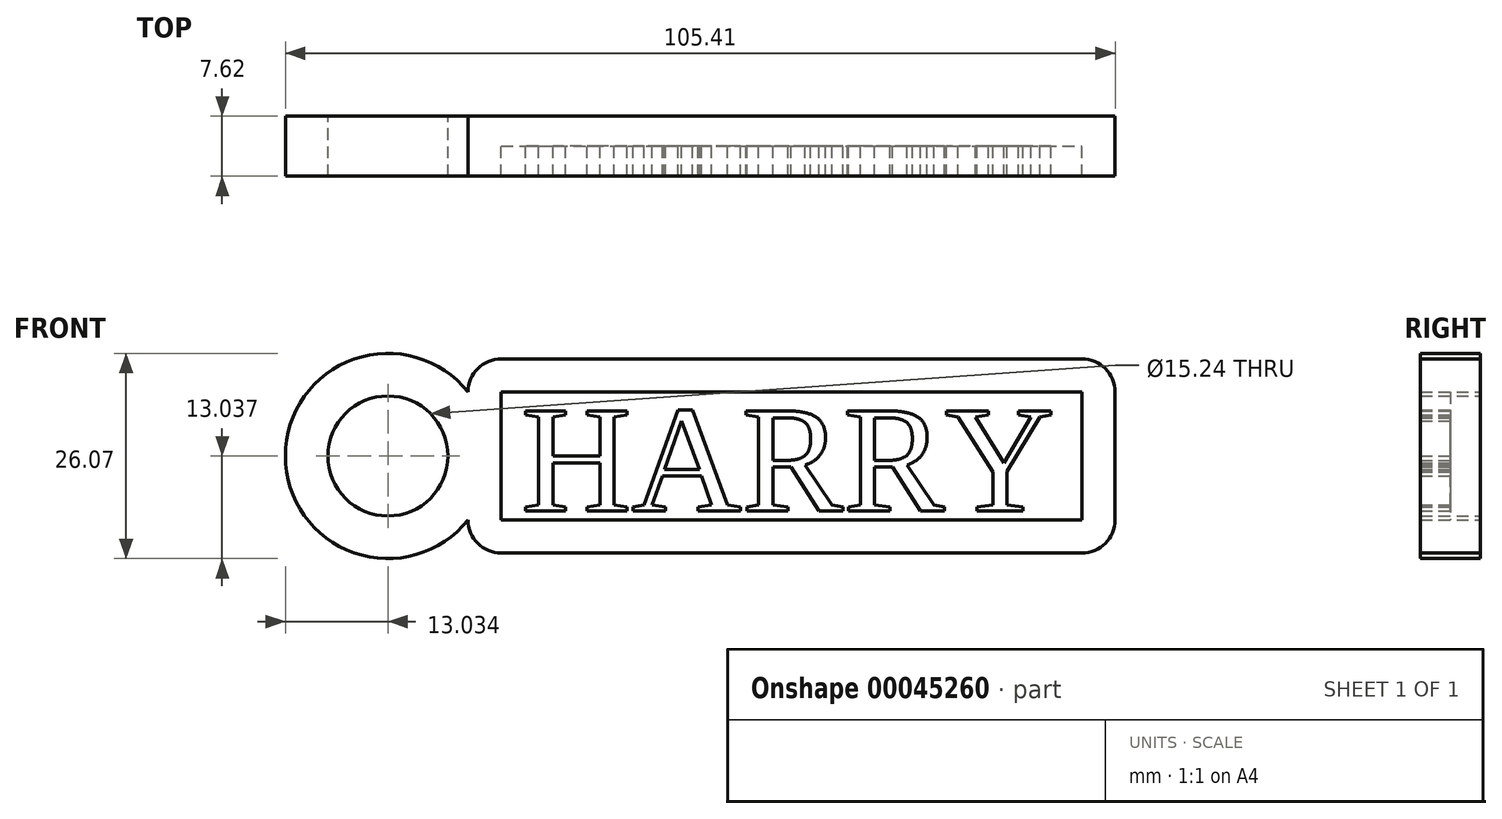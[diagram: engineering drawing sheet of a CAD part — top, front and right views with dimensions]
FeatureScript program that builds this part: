
annotation { "Feature Type Name" : "Feature", "Feature Type Description" : "" }
export const myFeature = defineFeature(function(context is Context, id is Id, definition is map)
    precondition{}
    {
        {
            var Q0;
            Q0=qCreatedBy(makeId("Front.planeOp"),FACE);
            var sketch = newSketch(context, id + "F0", { "sketchPlane" : qUnion([Q0])});
            skLineSegment(sketch, "E0.bottom", {"start": v(14.66, -24.69) * mm, "end": v(-59.1, -24.69) * mm});
            skLineSegment(sketch, "E0.top", {"start": v(14.66, 0) * mm, "end": v(-59.1, 0) * mm});
            skLineSegment(sketch, "E0.left", {"start": v(18.87, -20.47) * mm, "end": v(18.87, -4.21) * mm});
            skLineSegment(sketch, "E0.right", {"start": v(-63.32, -20.47) * mm, "end": v(-63.32, -4.21) * mm});
            skPoint(sketch, "E1.visualSharp", {"position": v(-63.32, 0) * mm});
            skArc(sketch, "E1.filletArc", {"start": v(-59.1, 0) * mm, "mid": v(-62.09, -1.23) * mm, "end": v(-63.32, -4.21) * mm});
            skPoint(sketch, "E2.visualSharp", {"position": v(-63.32, -24.69) * mm});
            skArc(sketch, "E2.filletArc", {"start": v(-63.32, -20.47) * mm, "mid": v(-62.09, -23.45) * mm, "end": v(-59.1, -24.69) * mm});
            skPoint(sketch, "E3.visualSharp", {"position": v(18.87, -24.69) * mm});
            skArc(sketch, "E3.filletArc", {"start": v(14.66, -24.69) * mm, "mid": v(17.63, -23.45) * mm, "end": v(18.87, -20.47) * mm});
            skPoint(sketch, "E4.visualSharp", {"position": v(18.87, 0) * mm});
            skArc(sketch, "E4.filletArc", {"start": v(18.87, -4.21) * mm, "mid": v(17.63, -1.23) * mm, "end": v(14.66, 0) * mm});
            skArc(sketch, "E5", {"start": v(-63.32, -4.21) * mm, "mid": v(-86.54, -12.34) * mm, "end": v(-63.32, -20.47) * mm});
            skSolve(sketch);
        }
        {
            var Q0;
            Q0=makeQuery(id+"F0.imprint","IMPRINT",FACE,{"disambiguationData":[TD([[makeQuery(id+"F0.imprint","IMPRINT",EDGE,{"derivedFrom":sQuery(id+"F0.wireOp",EDGE,"E0.bottom")}),-1.0]])]});
            extrude(context, id + "F1", {"entities" : qUnion([Q0]), "depth" : 3.8 * mm});
        }
        {
            var Q0;
            Q0=makeQuery(id+"F0.imprint","IMPRINT",FACE,{"disambiguationData":[TD([[makeQuery(id+"F0.imprint","IMPRINT",EDGE,{"derivedFrom":sQuery(id+"F0.wireOp",EDGE,"E0.right")}),1.0]])]});
            extrude(context, id + "F2", {"entities" : qUnion([Q0]), "operationType" : NewBodyOperationType.ADD, "depth" : 3.8 * mm});
        }
        {
            var Q0;
            Q0=sQuery(id+"F0.wireOp",VERTEX,"E5.center");
            var Q1;
            Q1=makeQuery(id+"F1.opExtrude","SWEPT_BODY",BODY,{"disambiguationData":[OSD([sQuery(id+"F0.wireOp",EDGE,"E0.bottom"),sQuery(id+"F0.wireOp",EDGE,"E0.top"),sQuery(id+"F0.wireOp",EDGE,"E0.left"),sQuery(id+"F0.wireOp",EDGE,"E0.right"),sQuery(id+"F0.wireOp",EDGE,"E1.filletArc"),sQuery(id+"F0.wireOp",EDGE,"E2.filletArc"),sQuery(id+"F0.wireOp",EDGE,"E3.filletArc"),sQuery(id+"F0.wireOp",EDGE,"E4.filletArc")])]});
            hole(context, id + "F3", {"style" : HoleStyle.SIMPLE, "holeDiameter" : 12.7 * mm, "endStyle" : HoleEndStyle.THROUGH, "oppositeDirection" : true, "locations" : qUnion([Q0]), "scope" : qUnion([Q1])});
        }
        {
            var Q0;
            {var subQ0=sQuery(id+"F0.wireOp",EDGE,"E0.right");Q0=makeQuery(id+"F2.boolean.opBoolean","MERGE",FACE,{"derivedFrom":[makeQuery(id+"F1.opExtrude","CAP_FACE",FACE,{"disambiguationData":[OSD([sQuery(id+"F0.wireOp",EDGE,"E0.bottom"),sQuery(id+"F0.wireOp",EDGE,"E0.top"),sQuery(id+"F0.wireOp",EDGE,"E0.left"),subQ0,sQuery(id+"F0.wireOp",EDGE,"E1.filletArc"),sQuery(id+"F0.wireOp",EDGE,"E2.filletArc"),sQuery(id+"F0.wireOp",EDGE,"E3.filletArc"),sQuery(id+"F0.wireOp",EDGE,"E4.filletArc")])],"isStart":false}),makeQuery(id+"F2.opExtrude","CAP_FACE",FACE,{"disambiguationData":[OSD([subQ0,sQuery(id+"F0.wireOp",EDGE,"E5")])],"isStart":false})]});}
            var sketch = newSketch(context, id + "F4", { "sketchPlane" : qUnion([Q0])});
            skLineSegment(sketch, "E6.bottom", {"start": v(-59.1, -4.21) * mm, "end": v(14.66, -4.21) * mm});
            skLineSegment(sketch, "E6.top", {"start": v(-59.1, -20.47) * mm, "end": v(14.66, -20.47) * mm});
            skLineSegment(sketch, "E6.left", {"start": v(-59.1, -4.21) * mm, "end": v(-59.1, -20.47) * mm});
            skLineSegment(sketch, "E6.right", {"start": v(14.66, -4.21) * mm, "end": v(14.66, -20.47) * mm});
            skSolve(sketch);
        }
        {
            var Q0;
            Q0=makeQuery(id+"F4.imprint","IMPRINT",FACE,{"disambiguationData":[TD([[makeQuery(id+"F4.imprint","IMPRINT",EDGE,{"derivedFrom":sQuery(id+"F4.wireOp",EDGE,"E6.bottom")}),1.0]])]});
            extrude(context, id + "F5", {"entities" : qUnion([Q0]), "operationType" : NewBodyOperationType.ADD, "depth" : 3.8 * mm});
        }
        {
            var Q0;
            Q0=qCreatedBy(makeId("Front.planeOp"),FACE);
            var sketch = newSketch(context, id + "F6", { "sketchPlane" : qUnion([Q0])});
            skText(sketch, "E7", { "text": "HARRY", "fontName": "Tinos-Regular.ttf"});
            const initialGuessF6  = {"E7": [-0.05657, -0.01931, 1, 0, 0.01394]};
            skSetInitialGuess(sketch, initialGuessF6);
            skSolve(sketch);
        }
        {
            var Q0;
            Q0 = qSketchRegion(id + "F6", true);
            extrude(context, id + "F7", {"entities" : qUnion([Q0]), "operationType" : NewBodyOperationType.ADD, "depth" : 3.8 * mm});
        }
        {
            var Q0;
            Q0 = qSketchRegion(id + "F6", true);
            var Q1;
            Q1=makeQuery(id+"F0.imprint","IMPRINT",FACE,{"disambiguationData":[TD([[makeQuery(id+"F0.imprint","IMPRINT",EDGE,{"derivedFrom":sQuery(id+"F0.wireOp",EDGE,"E0.right")}),1.0]])]});
            var Q2;
            Q2=makeQuery(id+"F5.opExtrude","CAP_FACE",FACE,{"disambiguationData":[OSD([sQuery(id+"F0.wireOp",EDGE,"E0.bottom"),sQuery(id+"F0.wireOp",EDGE,"E0.top"),sQuery(id+"F0.wireOp",EDGE,"E0.left"),sQuery(id+"F0.wireOp",EDGE,"E0.right"),sQuery(id+"F0.wireOp",EDGE,"E1.filletArc"),sQuery(id+"F0.wireOp",EDGE,"E2.filletArc"),sQuery(id+"F0.wireOp",EDGE,"E3.filletArc"),sQuery(id+"F0.wireOp",EDGE,"E4.filletArc"),sQuery(id+"F0.wireOp",EDGE,"E5"),sQuery(id+"F3.hole-0.sketch.wireOp",EDGE,"core_line_2"),sQuery(id+"F4.wireOp",EDGE,"E6.bottom"),sQuery(id+"F4.wireOp",EDGE,"E6.top"),sQuery(id+"F4.wireOp",EDGE,"E6.left"),sQuery(id+"F4.wireOp",EDGE,"E6.right")])],"isStart":false});
            extrude(context, id + "F8", {"entities" : qUnion([Q0, Q1]), "operationType" : NewBodyOperationType.ADD, "endBound" : BoundingType.UP_TO_SURFACE, "endBoundEntityFace" : qUnion([Q2]), "depth" : 3.8 * mm});
        }
        {
            var Q0;
            Q0=sQuery(id+"F0.wireOp",VERTEX,"E5.center");
            var Q1;
            Q1=makeQuery(id+"F1.opExtrude","SWEPT_BODY",BODY,{"disambiguationData":[OSD([sQuery(id+"F0.wireOp",EDGE,"E0.bottom"),sQuery(id+"F0.wireOp",EDGE,"E0.top"),sQuery(id+"F0.wireOp",EDGE,"E0.left"),sQuery(id+"F0.wireOp",EDGE,"E0.right"),sQuery(id+"F0.wireOp",EDGE,"E1.filletArc"),sQuery(id+"F0.wireOp",EDGE,"E2.filletArc"),sQuery(id+"F0.wireOp",EDGE,"E3.filletArc"),sQuery(id+"F0.wireOp",EDGE,"E4.filletArc")])]});
            hole(context, id + "F9", {"style" : HoleStyle.SIMPLE, "holeDiameter" : 15.24 * mm, "endStyle" : HoleEndStyle.THROUGH, "oppositeDirection" : true, "locations" : qUnion([Q0]), "scope" : qUnion([Q1])});
        }
    });
